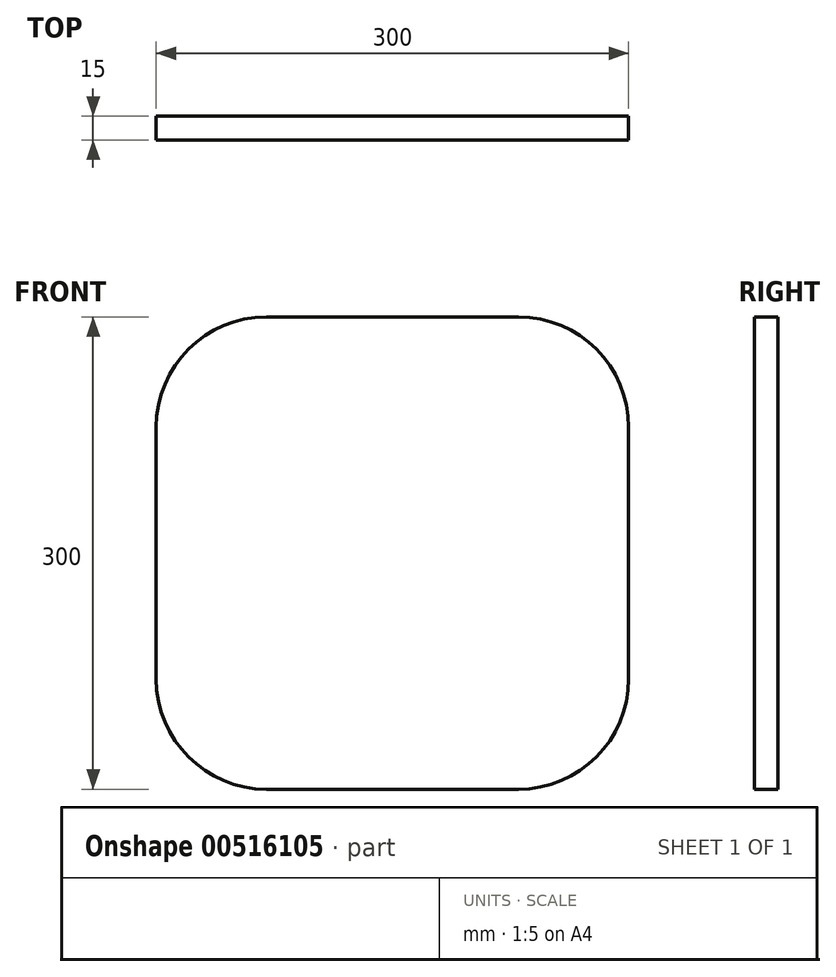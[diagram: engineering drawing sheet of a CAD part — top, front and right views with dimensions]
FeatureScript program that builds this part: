
annotation { "Feature Type Name" : "Feature", "Feature Type Description" : "" }
export const myFeature = defineFeature(function(context is Context, id is Id, definition is map)
    precondition{}
    {
        {
            var Q0;
            Q0=qCreatedBy(makeId("Front.planeOp"),FACE);
            var sketch = newSketch(context, id + "F0", { "sketchPlane" : qUnion([Q0])});
            skLineSegment(sketch, "E0.bottom", {"start": v(150, 150) * mm, "end": v(-150, 150) * mm});
            skLineSegment(sketch, "E0.top", {"start": v(150, -150) * mm, "end": v(-150, -150) * mm});
            skLineSegment(sketch, "E0.left", {"start": v(150, 150) * mm, "end": v(150, -150) * mm});
            skLineSegment(sketch, "E0.right", {"start": v(-150, 150) * mm, "end": v(-150, -150) * mm});
            skPoint(sketch, "E0.middle", {"position": v(0, 0) * mm});
            skSolve(sketch);
        }
        {
            var Q0;
            Q0 = qSketchRegion(id + "F0", true);
            extrude(context, id + "F1", {"entities" : qUnion([Q0]), "depth" : 15 * mm, "offsetDistance" : 25 * mm});
        }
        {
            var Q0;
            Q0=makeQuery(id+"F1.opExtrude","SWEPT_EDGE",EDGE,{"disambiguationData":[OSD([sQuery(id+"F0.wireOp",EDGE,"E0.bottom"),sQuery(id+"F0.wireOp",EDGE,"E0.left")])]});
            var Q1;
            Q1=makeQuery(id+"F1.opExtrude","SWEPT_EDGE",EDGE,{"disambiguationData":[OSD([sQuery(id+"F0.wireOp",EDGE,"E0.bottom"),sQuery(id+"F0.wireOp",EDGE,"E0.right")])]});
            var Q2;
            Q2=makeQuery(id+"F1.opExtrude","SWEPT_EDGE",EDGE,{"disambiguationData":[OSD([sQuery(id+"F0.wireOp",EDGE,"E0.top"),sQuery(id+"F0.wireOp",EDGE,"E0.right")])]});
            var Q3;
            Q3=makeQuery(id+"F1.opExtrude","SWEPT_EDGE",EDGE,{"disambiguationData":[OSD([sQuery(id+"F0.wireOp",EDGE,"E0.top"),sQuery(id+"F0.wireOp",EDGE,"E0.left")])]});
            fillet(context, id + "F2", {"entities" : qUnion([Q0, Q1, Q2, Q3]), "radius" : 70 * mm, "tangentPropagation" : true, "allowEdgeOverflow" : false});
        }
    });
